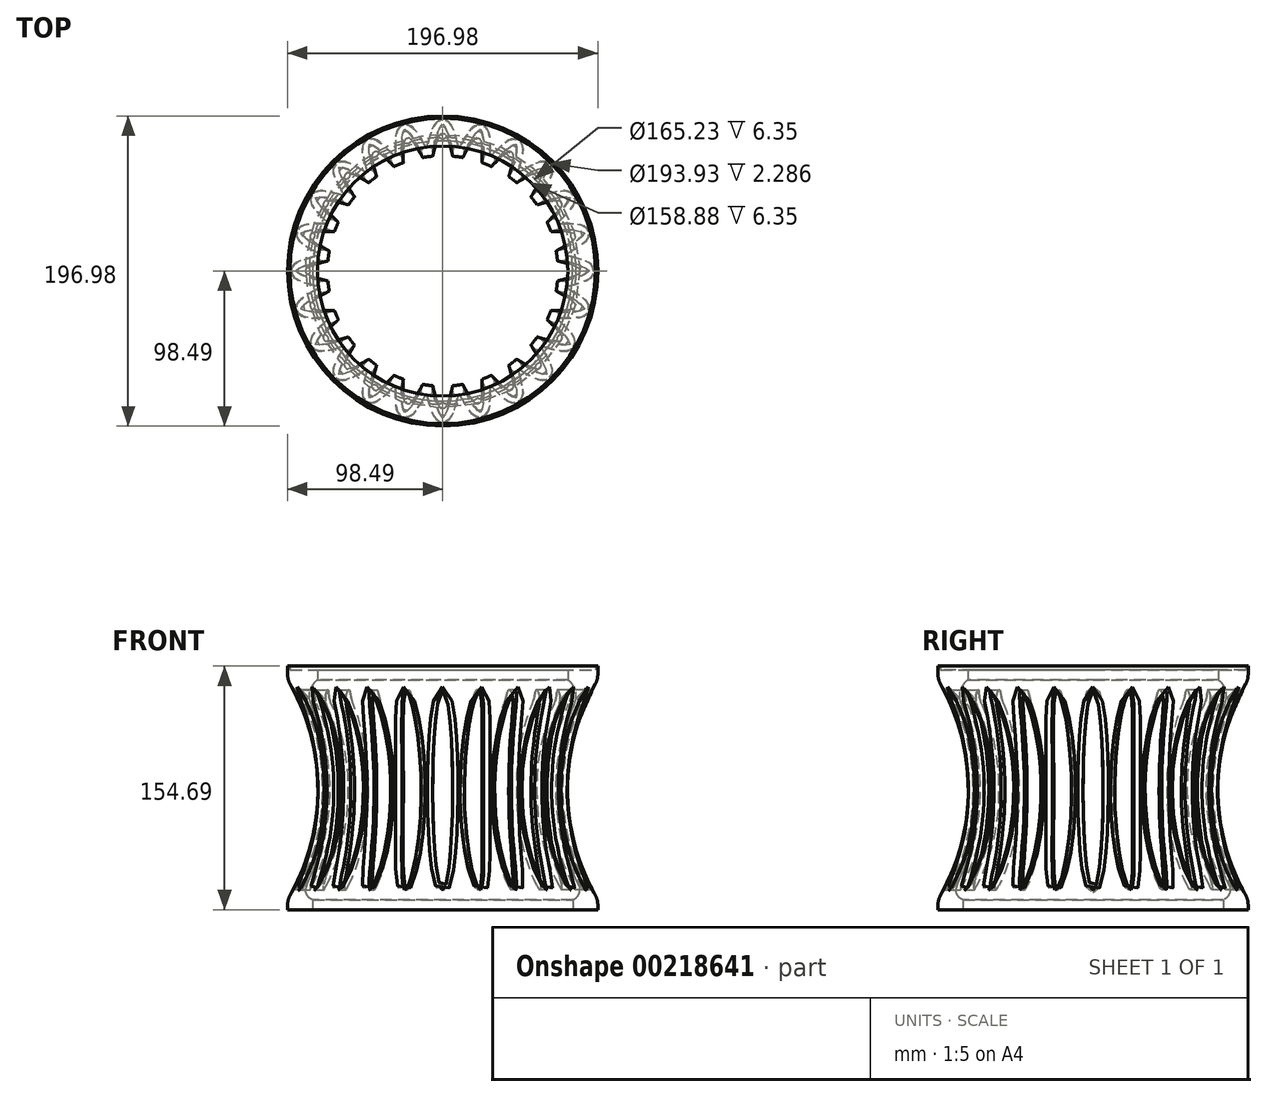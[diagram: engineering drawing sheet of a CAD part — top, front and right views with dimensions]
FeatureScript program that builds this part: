
annotation { "Feature Type Name" : "Feature", "Feature Type Description" : "" }
export const myFeature = defineFeature(function(context is Context, id is Id, definition is map)
    precondition{}
    {
        {
            var Q0;
            Q0=qCreatedBy(makeId("Front.planeOp"),FACE);
            var sketch = newSketch(context, id + "F0", { "sketchPlane" : qUnion([Q0])});
            skLineSegment(sketch, "E0", {"start": v(90.87, 146.05) * mm, "end": v(79.44, 146.05) * mm});
            skLineSegment(sketch, "E1", {"start": v(79.44, 146.05) * mm, "end": v(79.44, 152.4) * mm});
            skLineSegment(sketch, "E2", {"start": v(79.44, 152.4) * mm, "end": v(96.96, 152.4) * mm});
            skLineSegment(sketch, "E3", {"start": v(96.96, 152.4) * mm, "end": v(96.96, 154.69) * mm});
            skLineSegment(sketch, "E4", {"start": v(96.96, 154.69) * mm, "end": v(98.49, 154.69) * mm});
            skLineSegment(sketch, "E5", {"start": v(98.49, 0) * mm, "end": v(82.61, 0) * mm});
            skPoint(sketch, "E6", {"position": v(-98.49, 0) * mm});
            skLineSegment(sketch, "E7", {"start": v(90.87, 6.35) * mm, "end": v(82.61, 6.35) * mm});
            skLineSegment(sketch, "E8", {"start": v(82.61, 6.35) * mm, "end": v(82.61, 0) * mm});
            skArc(sketch, "E9", {"start": v(90.87, 146.05) * mm, "mid": v(73.17, 76.2) * mm, "end": v(90.87, 6.35) * mm});
            skArc(sketch, "E10", {"start": v(98.49, 146.05) * mm, "mid": v(79.82, 76.2) * mm, "end": v(98.49, 6.35) * mm});
            skLineSegment(sketch, "E11", {"start": v(98.49, 6.35) * mm, "end": v(98.49, 0) * mm});
            skLineSegment(sketch, "E12", {"start": v(98.49, 154.69) * mm, "end": v(98.49, 146.05) * mm});
            skLineSegment(sketch, "E13", {"start": v(0, 0) * mm, "end": v(0, 148.36) * mm});
            skSolve(sketch);
        }
        {
            var Q0;
            Q0 = qSketchRegion(id + "F0", true);
            var Q1;
            Q1=sQuery(id+"F0.wireOp",EDGE,"E13");
            revolve(context, id + "F1", {"entities" : qUnion([Q0]), "axis" : qUnion([Q1]), "revolveType" : RevolveType.FULL});
        }
        {
            var Q0;
            Q0=makeQuery(id+"F1.opRevolve","SWEPT_EDGE",EDGE,{"disambiguationData":[OSD([sQuery(id+"F0.wireOp",EDGE,"E0"),sQuery(id+"F0.wireOp",EDGE,"E9")])]});
            fillet(context, id + "F2", {"entities" : qUnion([Q0]), "radius" : 12.7 * mm, "tangentPropagation" : true, "allowEdgeOverflow" : false});
        }
        {
            var Q0;
            Q0=makeQuery(id+"F1.opRevolve","SWEPT_EDGE",EDGE,{"disambiguationData":[OSD([sQuery(id+"F0.wireOp",EDGE,"E7"),sQuery(id+"F0.wireOp",EDGE,"E9")])]});
            fillet(context, id + "F3", {"entities" : qUnion([Q0]), "radius" : 6.35 * mm, "tangentPropagation" : true, "allowEdgeOverflow" : false});
        }
        {
            var Q0;
            Q0=makeQuery(id+"F1.opRevolve","SWEPT_EDGE",EDGE,{"disambiguationData":[OSD([sQuery(id+"F0.wireOp",EDGE,"E10"),sQuery(id+"F0.wireOp",EDGE,"E12")])]});
            var Q1;
            Q1=makeQuery(id+"F1.opRevolve","SWEPT_EDGE",EDGE,{"disambiguationData":[OSD([sQuery(id+"F0.wireOp",EDGE,"E10"),sQuery(id+"F0.wireOp",EDGE,"E11")])]});
            fillet(context, id + "F4", {"entities" : qUnion([Q0, Q1]), "radius" : 12.7 * mm, "tangentPropagation" : true, "allowEdgeOverflow" : false});
        }
        {
            var Q0;
            Q0=sQuery(id+"F0.wireOp",EDGE,"E13");
            var Q1;
            Q1=qCreatedBy(makeId("Front.planeOp"),FACE);
            cPlane(context, id + "F5", {"entities" : qUnion([Q0, Q1]), "cplaneType" : CPlaneType.LINE_ANGLE, "offset" : 25.4 * mm, "angle" : 45 * degree, "width" : 152.4 * mm, "height" : 152.4 * mm});
        }
        {
            var Q0;
            Q0=qCreatedBy(id+"F5.planeOp",FACE);
            var sketch = newSketch(context, id + "F6", { "sketchPlane" : qUnion([Q0])});
            skEllipse(sketch, "E14", {"center": v(0, 76.2) * mm, "majorRadius": 63.5 * mm, "minorRadius": 6.35 * mm, "majorAxis": v(0, 1)});
            skSolve(sketch);
        }
        {
            var Q0;
            Q0 = qSketchRegion(id + "F6", true);
            extrude(context, id + "F7", {"entities" : qUnion([Q0]), "oppositeDirection" : true, "depth" : 101.6 * mm});
        }
        {
            var Q0;
            Q0=makeQuery(id+"F7.opExtrude","SWEPT_BODY",BODY,{"disambiguationData":[OSD([sQuery(id+"F6.wireOp",EDGE,"E14")])]});
            var Q1;
            Q1=sQuery(id+"F0.wireOp",EDGE,"E13");
            circularPattern(context, id + "F8", {"entities" : qUnion([Q0]), "axis" : qUnion([Q1]), "angle" : 360 * degree, "instanceCount" : 24, "equalSpace" : true});
        }
        {
            var Q0;
            Q0=makeQuery(id+"F8.opPattern","COPY",BODY,{"derivedFrom":makeQuery(id+"F7.opExtrude","SWEPT_BODY",BODY,{"disambiguationData":[OSD([sQuery(id+"F6.wireOp",EDGE,"E14")])]}),"instanceName":"23"});
            var Q1;
            Q1=makeQuery(id+"F7.opExtrude","SWEPT_BODY",BODY,{"disambiguationData":[OSD([sQuery(id+"F6.wireOp",EDGE,"E14")])]});
            var Q2;
            Q2=makeQuery(id+"F8.opPattern","COPY",BODY,{"derivedFrom":makeQuery(id+"F7.opExtrude","SWEPT_BODY",BODY,{"disambiguationData":[OSD([sQuery(id+"F6.wireOp",EDGE,"E14")])]}),"instanceName":"1"});
            var Q3;
            Q3=makeQuery(id+"F8.opPattern","COPY",BODY,{"derivedFrom":makeQuery(id+"F7.opExtrude","SWEPT_BODY",BODY,{"disambiguationData":[OSD([sQuery(id+"F6.wireOp",EDGE,"E14")])]}),"instanceName":"2"});
            var Q4;
            Q4=makeQuery(id+"F8.opPattern","COPY",BODY,{"derivedFrom":makeQuery(id+"F7.opExtrude","SWEPT_BODY",BODY,{"disambiguationData":[OSD([sQuery(id+"F6.wireOp",EDGE,"E14")])]}),"instanceName":"3"});
            var Q5;
            Q5=makeQuery(id+"F8.opPattern","COPY",BODY,{"derivedFrom":makeQuery(id+"F7.opExtrude","SWEPT_BODY",BODY,{"disambiguationData":[OSD([sQuery(id+"F6.wireOp",EDGE,"E14")])]}),"instanceName":"4"});
            var Q6;
            Q6=makeQuery(id+"F8.opPattern","COPY",BODY,{"derivedFrom":makeQuery(id+"F7.opExtrude","SWEPT_BODY",BODY,{"disambiguationData":[OSD([sQuery(id+"F6.wireOp",EDGE,"E14")])]}),"instanceName":"5"});
            var Q7;
            Q7=makeQuery(id+"F8.opPattern","COPY",BODY,{"derivedFrom":makeQuery(id+"F7.opExtrude","SWEPT_BODY",BODY,{"disambiguationData":[OSD([sQuery(id+"F6.wireOp",EDGE,"E14")])]}),"instanceName":"6"});
            var Q8;
            Q8=makeQuery(id+"F8.opPattern","COPY",BODY,{"derivedFrom":makeQuery(id+"F7.opExtrude","SWEPT_BODY",BODY,{"disambiguationData":[OSD([sQuery(id+"F6.wireOp",EDGE,"E14")])]}),"instanceName":"7"});
            var Q9;
            Q9=makeQuery(id+"F8.opPattern","COPY",BODY,{"derivedFrom":makeQuery(id+"F7.opExtrude","SWEPT_BODY",BODY,{"disambiguationData":[OSD([sQuery(id+"F6.wireOp",EDGE,"E14")])]}),"instanceName":"8"});
            var Q10;
            Q10=makeQuery(id+"F8.opPattern","COPY",BODY,{"derivedFrom":makeQuery(id+"F7.opExtrude","SWEPT_BODY",BODY,{"disambiguationData":[OSD([sQuery(id+"F6.wireOp",EDGE,"E14")])]}),"instanceName":"9"});
            var Q11;
            Q11=makeQuery(id+"F8.opPattern","COPY",BODY,{"derivedFrom":makeQuery(id+"F7.opExtrude","SWEPT_BODY",BODY,{"disambiguationData":[OSD([sQuery(id+"F6.wireOp",EDGE,"E14")])]}),"instanceName":"10"});
            var Q12;
            Q12=makeQuery(id+"F8.opPattern","COPY",BODY,{"derivedFrom":makeQuery(id+"F7.opExtrude","SWEPT_BODY",BODY,{"disambiguationData":[OSD([sQuery(id+"F6.wireOp",EDGE,"E14")])]}),"instanceName":"11"});
            var Q13;
            Q13=makeQuery(id+"F8.opPattern","COPY",BODY,{"derivedFrom":makeQuery(id+"F7.opExtrude","SWEPT_BODY",BODY,{"disambiguationData":[OSD([sQuery(id+"F6.wireOp",EDGE,"E14")])]}),"instanceName":"12"});
            var Q14;
            Q14=makeQuery(id+"F8.opPattern","COPY",BODY,{"derivedFrom":makeQuery(id+"F7.opExtrude","SWEPT_BODY",BODY,{"disambiguationData":[OSD([sQuery(id+"F6.wireOp",EDGE,"E14")])]}),"instanceName":"13"});
            var Q15;
            Q15=makeQuery(id+"F8.opPattern","COPY",BODY,{"derivedFrom":makeQuery(id+"F7.opExtrude","SWEPT_BODY",BODY,{"disambiguationData":[OSD([sQuery(id+"F6.wireOp",EDGE,"E14")])]}),"instanceName":"14"});
            var Q16;
            Q16=makeQuery(id+"F8.opPattern","COPY",BODY,{"derivedFrom":makeQuery(id+"F7.opExtrude","SWEPT_BODY",BODY,{"disambiguationData":[OSD([sQuery(id+"F6.wireOp",EDGE,"E14")])]}),"instanceName":"15"});
            var Q17;
            Q17=makeQuery(id+"F8.opPattern","COPY",BODY,{"derivedFrom":makeQuery(id+"F7.opExtrude","SWEPT_BODY",BODY,{"disambiguationData":[OSD([sQuery(id+"F6.wireOp",EDGE,"E14")])]}),"instanceName":"16"});
            var Q18;
            Q18=makeQuery(id+"F8.opPattern","COPY",BODY,{"derivedFrom":makeQuery(id+"F7.opExtrude","SWEPT_BODY",BODY,{"disambiguationData":[OSD([sQuery(id+"F6.wireOp",EDGE,"E14")])]}),"instanceName":"17"});
            var Q19;
            Q19=makeQuery(id+"F8.opPattern","COPY",BODY,{"derivedFrom":makeQuery(id+"F7.opExtrude","SWEPT_BODY",BODY,{"disambiguationData":[OSD([sQuery(id+"F6.wireOp",EDGE,"E14")])]}),"instanceName":"18"});
            var Q20;
            Q20=makeQuery(id+"F8.opPattern","COPY",BODY,{"derivedFrom":makeQuery(id+"F7.opExtrude","SWEPT_BODY",BODY,{"disambiguationData":[OSD([sQuery(id+"F6.wireOp",EDGE,"E14")])]}),"instanceName":"19"});
            var Q21;
            Q21=makeQuery(id+"F8.opPattern","COPY",BODY,{"derivedFrom":makeQuery(id+"F7.opExtrude","SWEPT_BODY",BODY,{"disambiguationData":[OSD([sQuery(id+"F6.wireOp",EDGE,"E14")])]}),"instanceName":"20"});
            var Q22;
            Q22=makeQuery(id+"F8.opPattern","COPY",BODY,{"derivedFrom":makeQuery(id+"F7.opExtrude","SWEPT_BODY",BODY,{"disambiguationData":[OSD([sQuery(id+"F6.wireOp",EDGE,"E14")])]}),"instanceName":"21"});
            var Q23;
            Q23=makeQuery(id+"F8.opPattern","COPY",BODY,{"derivedFrom":makeQuery(id+"F7.opExtrude","SWEPT_BODY",BODY,{"disambiguationData":[OSD([sQuery(id+"F6.wireOp",EDGE,"E14")])]}),"instanceName":"22"});
            var Q24;
            Q24=makeQuery(id+"F1.opRevolve","SWEPT_BODY",BODY,{"disambiguationData":[OSD([sQuery(id+"F0.wireOp",EDGE,"E0"),sQuery(id+"F0.wireOp",EDGE,"E1"),sQuery(id+"F0.wireOp",EDGE,"E2"),sQuery(id+"F0.wireOp",EDGE,"E3"),sQuery(id+"F0.wireOp",EDGE,"E4"),sQuery(id+"F0.wireOp",EDGE,"E5"),sQuery(id+"F0.wireOp",EDGE,"E7"),sQuery(id+"F0.wireOp",EDGE,"E8"),sQuery(id+"F0.wireOp",EDGE,"E9"),sQuery(id+"F0.wireOp",EDGE,"E10"),sQuery(id+"F0.wireOp",EDGE,"E11"),sQuery(id+"F0.wireOp",EDGE,"E12")])]});
            booleanBodies(context, id + "F9", {"operationType" : BooleanOperationType.SUBTRACTION, "tools" : qUnion([Q0, Q1, Q2, Q3, Q4, Q5, Q6, Q7, Q8, Q9, Q10, Q11, Q12, Q13, Q14, Q15, Q16, Q17, Q18, Q19, Q20, Q21, Q22, Q23]), "targets" : qUnion([Q24])});
        }
        {
            var Q0;
            Q0=makeQuery(id+"F9.opBoolean","INTERSECT",EDGE,{"derivedFrom":[makeQuery(id+"F1.opRevolve","SWEPT_FACE",FACE,{"disambiguationData":[OSD([sQuery(id+"F0.wireOp",EDGE,"E10")])]}),makeQuery(id+"F8.opPattern","COPY",FACE,{"derivedFrom":makeQuery(id+"F7.opExtrude","SWEPT_FACE",FACE,{"disambiguationData":[OSD([sQuery(id+"F6.wireOp",EDGE,"E14")])]}),"instanceName":"12"})]});
            var Q1;
            Q1=makeQuery(id+"F9.opBoolean","INTERSECT",EDGE,{"derivedFrom":[makeQuery(id+"F1.opRevolve","SWEPT_FACE",FACE,{"disambiguationData":[OSD([sQuery(id+"F0.wireOp",EDGE,"E10")])]}),makeQuery(id+"F8.opPattern","COPY",FACE,{"derivedFrom":makeQuery(id+"F7.opExtrude","SWEPT_FACE",FACE,{"disambiguationData":[OSD([sQuery(id+"F6.wireOp",EDGE,"E14")])]}),"instanceName":"13"})]});
            var Q2;
            Q2=makeQuery(id+"F9.opBoolean","INTERSECT",EDGE,{"derivedFrom":[makeQuery(id+"F1.opRevolve","SWEPT_FACE",FACE,{"disambiguationData":[OSD([sQuery(id+"F0.wireOp",EDGE,"E10")])]}),makeQuery(id+"F8.opPattern","COPY",FACE,{"derivedFrom":makeQuery(id+"F7.opExtrude","SWEPT_FACE",FACE,{"disambiguationData":[OSD([sQuery(id+"F6.wireOp",EDGE,"E14")])]}),"instanceName":"14"})]});
            var Q3;
            Q3=makeQuery(id+"F9.opBoolean","INTERSECT",EDGE,{"derivedFrom":[makeQuery(id+"F1.opRevolve","SWEPT_FACE",FACE,{"disambiguationData":[OSD([sQuery(id+"F0.wireOp",EDGE,"E10")])]}),makeQuery(id+"F8.opPattern","COPY",FACE,{"derivedFrom":makeQuery(id+"F7.opExtrude","SWEPT_FACE",FACE,{"disambiguationData":[OSD([sQuery(id+"F6.wireOp",EDGE,"E14")])]}),"instanceName":"15"})]});
            var Q4;
            Q4=makeQuery(id+"F9.opBoolean","INTERSECT",EDGE,{"derivedFrom":[makeQuery(id+"F1.opRevolve","SWEPT_FACE",FACE,{"disambiguationData":[OSD([sQuery(id+"F0.wireOp",EDGE,"E10")])]}),makeQuery(id+"F8.opPattern","COPY",FACE,{"derivedFrom":makeQuery(id+"F7.opExtrude","SWEPT_FACE",FACE,{"disambiguationData":[OSD([sQuery(id+"F6.wireOp",EDGE,"E14")])]}),"instanceName":"16"})]});
            var Q5;
            Q5=makeQuery(id+"F9.opBoolean","INTERSECT",EDGE,{"derivedFrom":[makeQuery(id+"F1.opRevolve","SWEPT_FACE",FACE,{"disambiguationData":[OSD([sQuery(id+"F0.wireOp",EDGE,"E10")])]}),makeQuery(id+"F8.opPattern","COPY",FACE,{"derivedFrom":makeQuery(id+"F7.opExtrude","SWEPT_FACE",FACE,{"disambiguationData":[OSD([sQuery(id+"F6.wireOp",EDGE,"E14")])]}),"instanceName":"17"})]});
            var Q6;
            Q6=makeQuery(id+"F9.opBoolean","INTERSECT",EDGE,{"derivedFrom":[makeQuery(id+"F1.opRevolve","SWEPT_FACE",FACE,{"disambiguationData":[OSD([sQuery(id+"F0.wireOp",EDGE,"E10")])]}),makeQuery(id+"F8.opPattern","COPY",FACE,{"derivedFrom":makeQuery(id+"F7.opExtrude","SWEPT_FACE",FACE,{"disambiguationData":[OSD([sQuery(id+"F6.wireOp",EDGE,"E14")])]}),"instanceName":"11"})]});
            var Q7;
            Q7=makeQuery(id+"F9.opBoolean","INTERSECT",EDGE,{"derivedFrom":[makeQuery(id+"F1.opRevolve","SWEPT_FACE",FACE,{"disambiguationData":[OSD([sQuery(id+"F0.wireOp",EDGE,"E10")])]}),makeQuery(id+"F8.opPattern","COPY",FACE,{"derivedFrom":makeQuery(id+"F7.opExtrude","SWEPT_FACE",FACE,{"disambiguationData":[OSD([sQuery(id+"F6.wireOp",EDGE,"E14")])]}),"instanceName":"10"})]});
            var Q8;
            Q8=makeQuery(id+"F9.opBoolean","INTERSECT",EDGE,{"derivedFrom":[makeQuery(id+"F1.opRevolve","SWEPT_FACE",FACE,{"disambiguationData":[OSD([sQuery(id+"F0.wireOp",EDGE,"E10")])]}),makeQuery(id+"F8.opPattern","COPY",FACE,{"derivedFrom":makeQuery(id+"F7.opExtrude","SWEPT_FACE",FACE,{"disambiguationData":[OSD([sQuery(id+"F6.wireOp",EDGE,"E14")])]}),"instanceName":"9"})]});
            var Q9;
            Q9=makeQuery(id+"F9.opBoolean","INTERSECT",EDGE,{"derivedFrom":[makeQuery(id+"F1.opRevolve","SWEPT_FACE",FACE,{"disambiguationData":[OSD([sQuery(id+"F0.wireOp",EDGE,"E10")])]}),makeQuery(id+"F8.opPattern","COPY",FACE,{"derivedFrom":makeQuery(id+"F7.opExtrude","SWEPT_FACE",FACE,{"disambiguationData":[OSD([sQuery(id+"F6.wireOp",EDGE,"E14")])]}),"instanceName":"8"})]});
            var Q10;
            Q10=makeQuery(id+"F9.opBoolean","INTERSECT",EDGE,{"derivedFrom":[makeQuery(id+"F1.opRevolve","SWEPT_FACE",FACE,{"disambiguationData":[OSD([sQuery(id+"F0.wireOp",EDGE,"E10")])]}),makeQuery(id+"F8.opPattern","COPY",FACE,{"derivedFrom":makeQuery(id+"F7.opExtrude","SWEPT_FACE",FACE,{"disambiguationData":[OSD([sQuery(id+"F6.wireOp",EDGE,"E14")])]}),"instanceName":"7"})]});
            var Q11;
            Q11=makeQuery(id+"F9.opBoolean","INTERSECT",EDGE,{"derivedFrom":[makeQuery(id+"F1.opRevolve","SWEPT_FACE",FACE,{"disambiguationData":[OSD([sQuery(id+"F0.wireOp",EDGE,"E10")])]}),makeQuery(id+"F8.opPattern","COPY",FACE,{"derivedFrom":makeQuery(id+"F7.opExtrude","SWEPT_FACE",FACE,{"disambiguationData":[OSD([sQuery(id+"F6.wireOp",EDGE,"E14")])]}),"instanceName":"6"})]});
            var Q12;
            Q12=makeQuery(id+"F9.opBoolean","INTERSECT",EDGE,{"derivedFrom":[makeQuery(id+"F1.opRevolve","SWEPT_FACE",FACE,{"disambiguationData":[OSD([sQuery(id+"F0.wireOp",EDGE,"E10")])]}),makeQuery(id+"F8.opPattern","COPY",FACE,{"derivedFrom":makeQuery(id+"F7.opExtrude","SWEPT_FACE",FACE,{"disambiguationData":[OSD([sQuery(id+"F6.wireOp",EDGE,"E14")])]}),"instanceName":"5"})]});
            var Q13;
            Q13=makeQuery(id+"F9.opBoolean","INTERSECT",EDGE,{"derivedFrom":[makeQuery(id+"F1.opRevolve","SWEPT_FACE",FACE,{"disambiguationData":[OSD([sQuery(id+"F0.wireOp",EDGE,"E10")])]}),makeQuery(id+"F8.opPattern","COPY",FACE,{"derivedFrom":makeQuery(id+"F7.opExtrude","SWEPT_FACE",FACE,{"disambiguationData":[OSD([sQuery(id+"F6.wireOp",EDGE,"E14")])]}),"instanceName":"4"})]});
            var Q14;
            Q14=makeQuery(id+"F9.opBoolean","INTERSECT",EDGE,{"derivedFrom":[makeQuery(id+"F1.opRevolve","SWEPT_FACE",FACE,{"disambiguationData":[OSD([sQuery(id+"F0.wireOp",EDGE,"E10")])]}),makeQuery(id+"F8.opPattern","COPY",FACE,{"derivedFrom":makeQuery(id+"F7.opExtrude","SWEPT_FACE",FACE,{"disambiguationData":[OSD([sQuery(id+"F6.wireOp",EDGE,"E14")])]}),"instanceName":"3"})]});
            var Q15;
            Q15=makeQuery(id+"F9.opBoolean","INTERSECT",EDGE,{"derivedFrom":[makeQuery(id+"F1.opRevolve","SWEPT_FACE",FACE,{"disambiguationData":[OSD([sQuery(id+"F0.wireOp",EDGE,"E10")])]}),makeQuery(id+"F8.opPattern","COPY",FACE,{"derivedFrom":makeQuery(id+"F7.opExtrude","SWEPT_FACE",FACE,{"disambiguationData":[OSD([sQuery(id+"F6.wireOp",EDGE,"E14")])]}),"instanceName":"2"})]});
            var Q16;
            Q16=makeQuery(id+"F9.opBoolean","INTERSECT",EDGE,{"derivedFrom":[makeQuery(id+"F1.opRevolve","SWEPT_FACE",FACE,{"disambiguationData":[OSD([sQuery(id+"F0.wireOp",EDGE,"E10")])]}),makeQuery(id+"F8.opPattern","COPY",FACE,{"derivedFrom":makeQuery(id+"F7.opExtrude","SWEPT_FACE",FACE,{"disambiguationData":[OSD([sQuery(id+"F6.wireOp",EDGE,"E14")])]}),"instanceName":"1"})]});
            var Q17;
            Q17=makeQuery(id+"F9.opBoolean","INTERSECT",EDGE,{"derivedFrom":[makeQuery(id+"F1.opRevolve","SWEPT_FACE",FACE,{"disambiguationData":[OSD([sQuery(id+"F0.wireOp",EDGE,"E10")])]}),makeQuery(id+"F7.opExtrude","SWEPT_FACE",FACE,{"disambiguationData":[OSD([sQuery(id+"F6.wireOp",EDGE,"E14")])]})]});
            var Q18;
            Q18=makeQuery(id+"F9.opBoolean","INTERSECT",EDGE,{"derivedFrom":[makeQuery(id+"F1.opRevolve","SWEPT_FACE",FACE,{"disambiguationData":[OSD([sQuery(id+"F0.wireOp",EDGE,"E10")])]}),makeQuery(id+"F8.opPattern","COPY",FACE,{"derivedFrom":makeQuery(id+"F7.opExtrude","SWEPT_FACE",FACE,{"disambiguationData":[OSD([sQuery(id+"F6.wireOp",EDGE,"E14")])]}),"instanceName":"23"})]});
            var Q19;
            Q19=makeQuery(id+"F9.opBoolean","INTERSECT",EDGE,{"derivedFrom":[makeQuery(id+"F1.opRevolve","SWEPT_FACE",FACE,{"disambiguationData":[OSD([sQuery(id+"F0.wireOp",EDGE,"E10")])]}),makeQuery(id+"F8.opPattern","COPY",FACE,{"derivedFrom":makeQuery(id+"F7.opExtrude","SWEPT_FACE",FACE,{"disambiguationData":[OSD([sQuery(id+"F6.wireOp",EDGE,"E14")])]}),"instanceName":"22"})]});
            var Q20;
            Q20=makeQuery(id+"F9.opBoolean","INTERSECT",EDGE,{"derivedFrom":[makeQuery(id+"F1.opRevolve","SWEPT_FACE",FACE,{"disambiguationData":[OSD([sQuery(id+"F0.wireOp",EDGE,"E10")])]}),makeQuery(id+"F8.opPattern","COPY",FACE,{"derivedFrom":makeQuery(id+"F7.opExtrude","SWEPT_FACE",FACE,{"disambiguationData":[OSD([sQuery(id+"F6.wireOp",EDGE,"E14")])]}),"instanceName":"21"})]});
            var Q21;
            Q21=makeQuery(id+"F9.opBoolean","INTERSECT",EDGE,{"derivedFrom":[makeQuery(id+"F1.opRevolve","SWEPT_FACE",FACE,{"disambiguationData":[OSD([sQuery(id+"F0.wireOp",EDGE,"E10")])]}),makeQuery(id+"F8.opPattern","COPY",FACE,{"derivedFrom":makeQuery(id+"F7.opExtrude","SWEPT_FACE",FACE,{"disambiguationData":[OSD([sQuery(id+"F6.wireOp",EDGE,"E14")])]}),"instanceName":"20"})]});
            var Q22;
            Q22=makeQuery(id+"F9.opBoolean","INTERSECT",EDGE,{"derivedFrom":[makeQuery(id+"F1.opRevolve","SWEPT_FACE",FACE,{"disambiguationData":[OSD([sQuery(id+"F0.wireOp",EDGE,"E10")])]}),makeQuery(id+"F8.opPattern","COPY",FACE,{"derivedFrom":makeQuery(id+"F7.opExtrude","SWEPT_FACE",FACE,{"disambiguationData":[OSD([sQuery(id+"F6.wireOp",EDGE,"E14")])]}),"instanceName":"19"})]});
            var Q23;
            Q23=makeQuery(id+"F9.opBoolean","INTERSECT",EDGE,{"derivedFrom":[makeQuery(id+"F1.opRevolve","SWEPT_FACE",FACE,{"disambiguationData":[OSD([sQuery(id+"F0.wireOp",EDGE,"E10")])]}),makeQuery(id+"F8.opPattern","COPY",FACE,{"derivedFrom":makeQuery(id+"F7.opExtrude","SWEPT_FACE",FACE,{"disambiguationData":[OSD([sQuery(id+"F6.wireOp",EDGE,"E14")])]}),"instanceName":"18"})]});
            fillet(context, id + "F10", {"entities" : qUnion([Q0, Q1, Q2, Q3, Q4, Q5, Q6, Q7, Q8, Q9, Q10, Q11, Q12, Q13, Q14, Q15, Q16, Q17, Q18, Q19, Q20, Q21, Q22, Q23]), "radius" : 3.05 * mm, "tangentPropagation" : true, "allowEdgeOverflow" : false});
        }
    });
